# Revit family: ARON_EdgeT1-4FA Family
name_source: partatom
category: Lighting Fixtures
units: mm (PartAtom-declared; Revit-internal decimal feet)

## family parameters
Cut with Voids When Loaded = No
Host = Face
Light Source = Yes
Part Type = Normal
Room Calculation Point = No
Round Connector Dimension = Use Diameter
Shared = No

## types (3) — shared parameters
Color Filter = 16777215
Default Elevation = 4' - 0"
Dimming Lamp Color Temperature Shift = <None>
Emit Shape Visible in Rendering = Yes
Emit from Rectangle Length = 3' - 11 3/8"
Emit from Rectangle Width = 0' - 2 3/32"
Housing Material = White Painted Aluminum
Illuminated Surface Material = Frosted Acrylic Lens
Tilt Angle = 90.00°
Voltage = 120 V

## per-type parameters (varying)
| type | Apparent Load | Photometric Web File |
| EdgeT1-F-RTB-4FA-450-B1-35K8-UNV-DM-W | 18 VA | EdgeT1-F-RTB-4FA-450-B1-35K8-UNV-DM-W.ies |
| EdgeT1-F-RTB-4FA-650-B1-35K8-UNV-DM-W | 22 VA | EdgeT1-F-RTB-4FA-650-B1-35K8-UNV-DM-W.ies |
| EdgeT1-F-RTB-4FA-850-B1-35K8-UNV-DM-W | 36 VA | EdgeT1-F-RTB-4FA-850-B1-35K8-UNV-DM-W.ies |

## geometry (parser evidence)
native form markers: Extrusion x1, Sweep x1
no freeform markers — native parametric forms only
